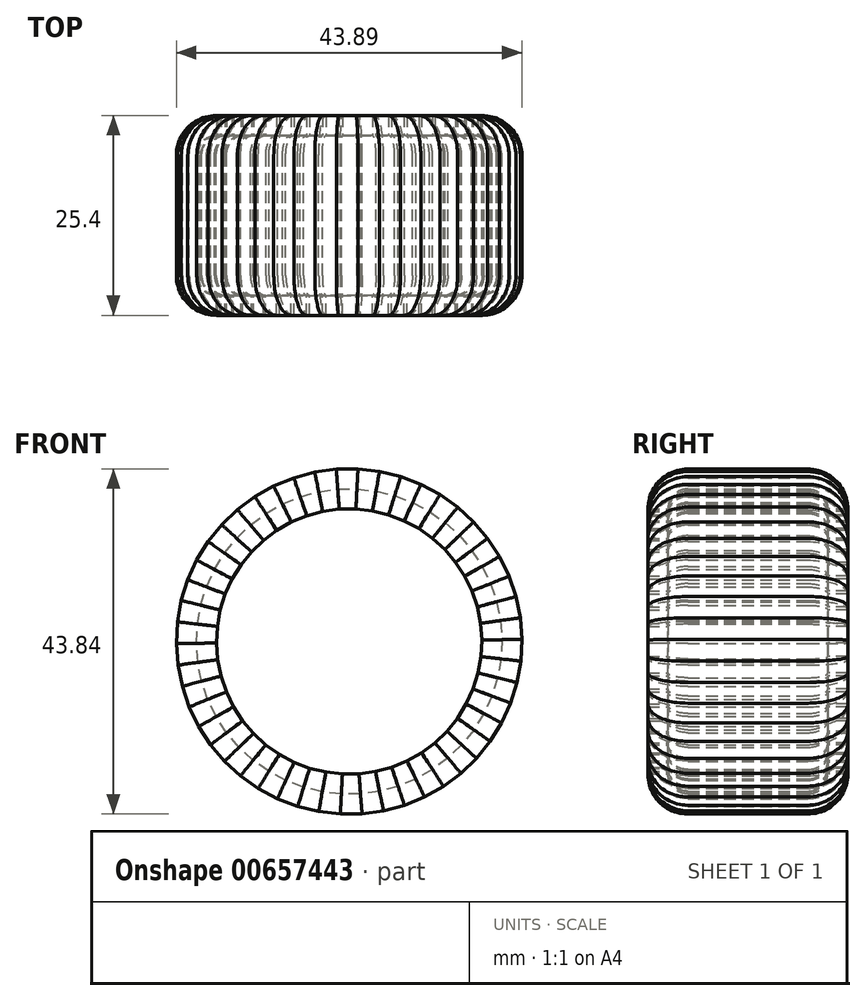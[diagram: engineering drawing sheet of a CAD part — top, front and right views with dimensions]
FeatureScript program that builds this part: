
annotation { "Feature Type Name" : "Feature", "Feature Type Description" : "" }
export const myFeature = defineFeature(function(context is Context, id is Id, definition is map)
    precondition{}
    {
        {
            var Q0;
            Q0=qCreatedBy(makeId("Front.planeOp"),FACE);
            var sketch = newSketch(context, id + "F0", { "sketchPlane" : qUnion([Q0])});
            skCircle(sketch, "E0.cCircle", {"center": v(-63.85, 53.38) * mm, "radius": 21.95 * mm, "construction": true});
            skLineSegment(sketch, "E0.0", {"start": v(-49.66, 36.63) * mm, "end": v(-51.87, 34.99) * mm});
            skLineSegment(sketch, "E0.1", {"start": v(-51.87, 34.99) * mm, "end": v(-54.27, 33.63) * mm});
            skLineSegment(sketch, "E0.2", {"start": v(-54.27, 33.63) * mm, "end": v(-56.82, 32.59) * mm});
            skLineSegment(sketch, "E0.3", {"start": v(-56.82, 32.59) * mm, "end": v(-59.48, 31.87) * mm});
            skLineSegment(sketch, "E0.4", {"start": v(-59.48, 31.87) * mm, "end": v(-62.21, 31.5) * mm});
            skLineSegment(sketch, "E0.5", {"start": v(-62.21, 31.5) * mm, "end": v(-64.97, 31.46) * mm});
            skLineSegment(sketch, "E0.6", {"start": v(-64.97, 31.46) * mm, "end": v(-67.7, 31.77) * mm});
            skLineSegment(sketch, "E0.7", {"start": v(-67.7, 31.77) * mm, "end": v(-70.38, 32.43) * mm});
            skLineSegment(sketch, "E0.8", {"start": v(-70.38, 32.43) * mm, "end": v(-72.96, 33.41) * mm});
            skLineSegment(sketch, "E0.9", {"start": v(-72.96, 33.41) * mm, "end": v(-75.39, 34.71) * mm});
            skLineSegment(sketch, "E0.10", {"start": v(-75.39, 34.71) * mm, "end": v(-77.64, 36.3) * mm});
            skLineSegment(sketch, "E0.11", {"start": v(-77.64, 36.3) * mm, "end": v(-79.67, 38.17) * mm});
            skLineSegment(sketch, "E0.12", {"start": v(-79.67, 38.17) * mm, "end": v(-81.45, 40.27) * mm});
            skLineSegment(sketch, "E0.13", {"start": v(-81.45, 40.27) * mm, "end": v(-82.95, 42.58) * mm});
            skLineSegment(sketch, "E0.14", {"start": v(-82.95, 42.58) * mm, "end": v(-84.16, 45.06) * mm});
            skLineSegment(sketch, "E0.15", {"start": v(-84.16, 45.06) * mm, "end": v(-85.04, 47.67) * mm});
            skLineSegment(sketch, "E0.16", {"start": v(-85.04, 47.67) * mm, "end": v(-85.59, 50.37) * mm});
            skLineSegment(sketch, "E0.17", {"start": v(-85.59, 50.37) * mm, "end": v(-85.8, 53.12) * mm});
            skLineSegment(sketch, "E0.18", {"start": v(-85.8, 53.12) * mm, "end": v(-85.65, 55.87) * mm});
            skLineSegment(sketch, "E0.19", {"start": v(-85.65, 55.87) * mm, "end": v(-85.17, 58.59) * mm});
            skLineSegment(sketch, "E0.20", {"start": v(-85.17, 58.59) * mm, "end": v(-84.35, 61.22) * mm});
            skLineSegment(sketch, "E0.21", {"start": v(-84.35, 61.22) * mm, "end": v(-83.2, 63.73) * mm});
            skLineSegment(sketch, "E0.22", {"start": v(-83.2, 63.73) * mm, "end": v(-81.75, 66.07) * mm});
            skLineSegment(sketch, "E0.23", {"start": v(-81.75, 66.07) * mm, "end": v(-80.02, 68.21) * mm});
            skLineSegment(sketch, "E0.24", {"start": v(-80.02, 68.21) * mm, "end": v(-78.03, 70.13) * mm});
            skLineSegment(sketch, "E0.25", {"start": v(-78.03, 70.13) * mm, "end": v(-75.82, 71.77) * mm});
            skLineSegment(sketch, "E0.26", {"start": v(-75.82, 71.77) * mm, "end": v(-73.42, 73.13) * mm});
            skLineSegment(sketch, "E0.27", {"start": v(-73.42, 73.13) * mm, "end": v(-70.87, 74.17) * mm});
            skLineSegment(sketch, "E0.28", {"start": v(-70.87, 74.17) * mm, "end": v(-68.21, 74.89) * mm});
            skLineSegment(sketch, "E0.29", {"start": v(-68.21, 74.89) * mm, "end": v(-65.48, 75.27) * mm});
            skLineSegment(sketch, "E0.30", {"start": v(-65.48, 75.27) * mm, "end": v(-62.72, 75.3) * mm});
            skLineSegment(sketch, "E0.31", {"start": v(-62.72, 75.3) * mm, "end": v(-59.99, 74.99) * mm});
            skLineSegment(sketch, "E0.32", {"start": v(-59.99, 74.99) * mm, "end": v(-57.3, 74.33) * mm});
            skLineSegment(sketch, "E0.33", {"start": v(-57.3, 74.33) * mm, "end": v(-54.73, 73.35) * mm});
            skLineSegment(sketch, "E0.34", {"start": v(-54.73, 73.35) * mm, "end": v(-52.3, 72.05) * mm});
            skLineSegment(sketch, "E0.35", {"start": v(-52.3, 72.05) * mm, "end": v(-50.05, 70.45) * mm});
            skLineSegment(sketch, "E0.36", {"start": v(-50.05, 70.45) * mm, "end": v(-48.02, 68.6) * mm});
            skLineSegment(sketch, "E0.37", {"start": v(-48.02, 68.6) * mm, "end": v(-46.24, 66.49) * mm});
            skLineSegment(sketch, "E0.38", {"start": v(-46.24, 66.49) * mm, "end": v(-44.74, 64.18) * mm});
            skLineSegment(sketch, "E0.39", {"start": v(-44.74, 64.18) * mm, "end": v(-43.53, 61.7) * mm});
            skLineSegment(sketch, "E0.40", {"start": v(-43.53, 61.7) * mm, "end": v(-42.65, 59.09) * mm});
            skLineSegment(sketch, "E0.41", {"start": v(-42.65, 59.09) * mm, "end": v(-42.1, 56.38) * mm});
            skLineSegment(sketch, "E0.42", {"start": v(-42.1, 56.38) * mm, "end": v(-41.9, 53.64) * mm});
            skLineSegment(sketch, "E0.43", {"start": v(-41.9, 53.64) * mm, "end": v(-42.04, 50.88) * mm});
            skLineSegment(sketch, "E0.44", {"start": v(-42.04, 50.88) * mm, "end": v(-42.52, 48.17) * mm});
            skLineSegment(sketch, "E0.45", {"start": v(-42.52, 48.17) * mm, "end": v(-43.34, 45.54) * mm});
            skLineSegment(sketch, "E0.46", {"start": v(-43.34, 45.54) * mm, "end": v(-44.49, 43.03) * mm});
            skLineSegment(sketch, "E0.47", {"start": v(-44.49, 43.03) * mm, "end": v(-45.94, 40.69) * mm});
            skLineSegment(sketch, "E0.48", {"start": v(-45.94, 40.69) * mm, "end": v(-47.67, 38.54) * mm});
            skLineSegment(sketch, "E0.49", {"start": v(-47.67, 38.54) * mm, "end": v(-49.66, 36.63) * mm});
            skSolve(sketch);
        }
        {
            var Q0;
            Q0 = qSketchRegion(id + "F0", true);
            extrude(context, id + "F1", {"entities" : qUnion([Q0]), "depth" : 25.4 * mm, "offsetDistance" : 25.4 * mm});
        }
        {
            var Q0;
            Q0=makeQuery(id+"F1.opExtrude","CAP_FACE",FACE,{"disambiguationData":[OSD([sQuery(id+"F0.wireOp",EDGE,"E0.0"),sQuery(id+"F0.wireOp",EDGE,"E0.1"),sQuery(id+"F0.wireOp",EDGE,"E0.2"),sQuery(id+"F0.wireOp",EDGE,"E0.3"),sQuery(id+"F0.wireOp",EDGE,"E0.4"),sQuery(id+"F0.wireOp",EDGE,"E0.5"),sQuery(id+"F0.wireOp",EDGE,"E0.6"),sQuery(id+"F0.wireOp",EDGE,"E0.7"),sQuery(id+"F0.wireOp",EDGE,"E0.8"),sQuery(id+"F0.wireOp",EDGE,"E0.9"),sQuery(id+"F0.wireOp",EDGE,"E0.10"),sQuery(id+"F0.wireOp",EDGE,"E0.11"),sQuery(id+"F0.wireOp",EDGE,"E0.12"),sQuery(id+"F0.wireOp",EDGE,"E0.13"),sQuery(id+"F0.wireOp",EDGE,"E0.14"),sQuery(id+"F0.wireOp",EDGE,"E0.15"),sQuery(id+"F0.wireOp",EDGE,"E0.16"),sQuery(id+"F0.wireOp",EDGE,"E0.17"),sQuery(id+"F0.wireOp",EDGE,"E0.18"),sQuery(id+"F0.wireOp",EDGE,"E0.19"),sQuery(id+"F0.wireOp",EDGE,"E0.20"),sQuery(id+"F0.wireOp",EDGE,"E0.21"),sQuery(id+"F0.wireOp",EDGE,"E0.22"),sQuery(id+"F0.wireOp",EDGE,"E0.23"),sQuery(id+"F0.wireOp",EDGE,"E0.24"),sQuery(id+"F0.wireOp",EDGE,"E0.25"),sQuery(id+"F0.wireOp",EDGE,"E0.26"),sQuery(id+"F0.wireOp",EDGE,"E0.27"),sQuery(id+"F0.wireOp",EDGE,"E0.28"),sQuery(id+"F0.wireOp",EDGE,"E0.29"),sQuery(id+"F0.wireOp",EDGE,"E0.30"),sQuery(id+"F0.wireOp",EDGE,"E0.31"),sQuery(id+"F0.wireOp",EDGE,"E0.32"),sQuery(id+"F0.wireOp",EDGE,"E0.33"),sQuery(id+"F0.wireOp",EDGE,"E0.34"),sQuery(id+"F0.wireOp",EDGE,"E0.35"),sQuery(id+"F0.wireOp",EDGE,"E0.36"),sQuery(id+"F0.wireOp",EDGE,"E0.37"),sQuery(id+"F0.wireOp",EDGE,"E0.38"),sQuery(id+"F0.wireOp",EDGE,"E0.39"),sQuery(id+"F0.wireOp",EDGE,"E0.40"),sQuery(id+"F0.wireOp",EDGE,"E0.41"),sQuery(id+"F0.wireOp",EDGE,"E0.42"),sQuery(id+"F0.wireOp",EDGE,"E0.43"),sQuery(id+"F0.wireOp",EDGE,"E0.44"),sQuery(id+"F0.wireOp",EDGE,"E0.45"),sQuery(id+"F0.wireOp",EDGE,"E0.46"),sQuery(id+"F0.wireOp",EDGE,"E0.47"),sQuery(id+"F0.wireOp",EDGE,"E0.48"),sQuery(id+"F0.wireOp",EDGE,"E0.49")])],"isStart":false});
            var Q1;
            Q1=makeQuery(id+"F1.opExtrude","CAP_FACE",FACE,{"disambiguationData":[OSD([sQuery(id+"F0.wireOp",EDGE,"E0.0"),sQuery(id+"F0.wireOp",EDGE,"E0.1"),sQuery(id+"F0.wireOp",EDGE,"E0.2"),sQuery(id+"F0.wireOp",EDGE,"E0.3"),sQuery(id+"F0.wireOp",EDGE,"E0.4"),sQuery(id+"F0.wireOp",EDGE,"E0.5"),sQuery(id+"F0.wireOp",EDGE,"E0.6"),sQuery(id+"F0.wireOp",EDGE,"E0.7"),sQuery(id+"F0.wireOp",EDGE,"E0.8"),sQuery(id+"F0.wireOp",EDGE,"E0.9"),sQuery(id+"F0.wireOp",EDGE,"E0.10"),sQuery(id+"F0.wireOp",EDGE,"E0.11"),sQuery(id+"F0.wireOp",EDGE,"E0.12"),sQuery(id+"F0.wireOp",EDGE,"E0.13"),sQuery(id+"F0.wireOp",EDGE,"E0.14"),sQuery(id+"F0.wireOp",EDGE,"E0.15"),sQuery(id+"F0.wireOp",EDGE,"E0.16"),sQuery(id+"F0.wireOp",EDGE,"E0.17"),sQuery(id+"F0.wireOp",EDGE,"E0.18"),sQuery(id+"F0.wireOp",EDGE,"E0.19"),sQuery(id+"F0.wireOp",EDGE,"E0.20"),sQuery(id+"F0.wireOp",EDGE,"E0.21"),sQuery(id+"F0.wireOp",EDGE,"E0.22"),sQuery(id+"F0.wireOp",EDGE,"E0.23"),sQuery(id+"F0.wireOp",EDGE,"E0.24"),sQuery(id+"F0.wireOp",EDGE,"E0.25"),sQuery(id+"F0.wireOp",EDGE,"E0.26"),sQuery(id+"F0.wireOp",EDGE,"E0.27"),sQuery(id+"F0.wireOp",EDGE,"E0.28"),sQuery(id+"F0.wireOp",EDGE,"E0.29"),sQuery(id+"F0.wireOp",EDGE,"E0.30"),sQuery(id+"F0.wireOp",EDGE,"E0.31"),sQuery(id+"F0.wireOp",EDGE,"E0.32"),sQuery(id+"F0.wireOp",EDGE,"E0.33"),sQuery(id+"F0.wireOp",EDGE,"E0.34"),sQuery(id+"F0.wireOp",EDGE,"E0.35"),sQuery(id+"F0.wireOp",EDGE,"E0.36"),sQuery(id+"F0.wireOp",EDGE,"E0.37"),sQuery(id+"F0.wireOp",EDGE,"E0.38"),sQuery(id+"F0.wireOp",EDGE,"E0.39"),sQuery(id+"F0.wireOp",EDGE,"E0.40"),sQuery(id+"F0.wireOp",EDGE,"E0.41"),sQuery(id+"F0.wireOp",EDGE,"E0.42"),sQuery(id+"F0.wireOp",EDGE,"E0.43"),sQuery(id+"F0.wireOp",EDGE,"E0.44"),sQuery(id+"F0.wireOp",EDGE,"E0.45"),sQuery(id+"F0.wireOp",EDGE,"E0.46"),sQuery(id+"F0.wireOp",EDGE,"E0.47"),sQuery(id+"F0.wireOp",EDGE,"E0.48"),sQuery(id+"F0.wireOp",EDGE,"E0.49")])],"isStart":true});
            fillet(context, id + "F2", {"entities" : qUnion([Q0, Q1]), "radius" : 5.08 * mm, "tangentPropagation" : true, "allowEdgeOverflow" : false});
        }
        {
            var Q0;
            Q0=makeQuery(id+"F1.opExtrude","CAP_FACE",FACE,{"disambiguationData":[OSD([sQuery(id+"F0.wireOp",EDGE,"E0.0"),sQuery(id+"F0.wireOp",EDGE,"E0.1"),sQuery(id+"F0.wireOp",EDGE,"E0.2"),sQuery(id+"F0.wireOp",EDGE,"E0.3"),sQuery(id+"F0.wireOp",EDGE,"E0.4"),sQuery(id+"F0.wireOp",EDGE,"E0.5"),sQuery(id+"F0.wireOp",EDGE,"E0.6"),sQuery(id+"F0.wireOp",EDGE,"E0.7"),sQuery(id+"F0.wireOp",EDGE,"E0.8"),sQuery(id+"F0.wireOp",EDGE,"E0.9"),sQuery(id+"F0.wireOp",EDGE,"E0.10"),sQuery(id+"F0.wireOp",EDGE,"E0.11"),sQuery(id+"F0.wireOp",EDGE,"E0.12"),sQuery(id+"F0.wireOp",EDGE,"E0.13"),sQuery(id+"F0.wireOp",EDGE,"E0.14"),sQuery(id+"F0.wireOp",EDGE,"E0.15"),sQuery(id+"F0.wireOp",EDGE,"E0.16"),sQuery(id+"F0.wireOp",EDGE,"E0.17"),sQuery(id+"F0.wireOp",EDGE,"E0.18"),sQuery(id+"F0.wireOp",EDGE,"E0.19"),sQuery(id+"F0.wireOp",EDGE,"E0.20"),sQuery(id+"F0.wireOp",EDGE,"E0.21"),sQuery(id+"F0.wireOp",EDGE,"E0.22"),sQuery(id+"F0.wireOp",EDGE,"E0.23"),sQuery(id+"F0.wireOp",EDGE,"E0.24"),sQuery(id+"F0.wireOp",EDGE,"E0.25"),sQuery(id+"F0.wireOp",EDGE,"E0.26"),sQuery(id+"F0.wireOp",EDGE,"E0.27"),sQuery(id+"F0.wireOp",EDGE,"E0.28"),sQuery(id+"F0.wireOp",EDGE,"E0.29"),sQuery(id+"F0.wireOp",EDGE,"E0.30"),sQuery(id+"F0.wireOp",EDGE,"E0.31"),sQuery(id+"F0.wireOp",EDGE,"E0.32"),sQuery(id+"F0.wireOp",EDGE,"E0.33"),sQuery(id+"F0.wireOp",EDGE,"E0.34"),sQuery(id+"F0.wireOp",EDGE,"E0.35"),sQuery(id+"F0.wireOp",EDGE,"E0.36"),sQuery(id+"F0.wireOp",EDGE,"E0.37"),sQuery(id+"F0.wireOp",EDGE,"E0.38"),sQuery(id+"F0.wireOp",EDGE,"E0.39"),sQuery(id+"F0.wireOp",EDGE,"E0.40"),sQuery(id+"F0.wireOp",EDGE,"E0.41"),sQuery(id+"F0.wireOp",EDGE,"E0.42"),sQuery(id+"F0.wireOp",EDGE,"E0.43"),sQuery(id+"F0.wireOp",EDGE,"E0.44"),sQuery(id+"F0.wireOp",EDGE,"E0.45"),sQuery(id+"F0.wireOp",EDGE,"E0.46"),sQuery(id+"F0.wireOp",EDGE,"E0.47"),sQuery(id+"F0.wireOp",EDGE,"E0.48"),sQuery(id+"F0.wireOp",EDGE,"E0.49")])],"isStart":false});
            var Q1;
            Q1=makeQuery(id+"F1.opExtrude","CAP_FACE",FACE,{"disambiguationData":[OSD([sQuery(id+"F0.wireOp",EDGE,"E0.0"),sQuery(id+"F0.wireOp",EDGE,"E0.1"),sQuery(id+"F0.wireOp",EDGE,"E0.2"),sQuery(id+"F0.wireOp",EDGE,"E0.3"),sQuery(id+"F0.wireOp",EDGE,"E0.4"),sQuery(id+"F0.wireOp",EDGE,"E0.5"),sQuery(id+"F0.wireOp",EDGE,"E0.6"),sQuery(id+"F0.wireOp",EDGE,"E0.7"),sQuery(id+"F0.wireOp",EDGE,"E0.8"),sQuery(id+"F0.wireOp",EDGE,"E0.9"),sQuery(id+"F0.wireOp",EDGE,"E0.10"),sQuery(id+"F0.wireOp",EDGE,"E0.11"),sQuery(id+"F0.wireOp",EDGE,"E0.12"),sQuery(id+"F0.wireOp",EDGE,"E0.13"),sQuery(id+"F0.wireOp",EDGE,"E0.14"),sQuery(id+"F0.wireOp",EDGE,"E0.15"),sQuery(id+"F0.wireOp",EDGE,"E0.16"),sQuery(id+"F0.wireOp",EDGE,"E0.17"),sQuery(id+"F0.wireOp",EDGE,"E0.18"),sQuery(id+"F0.wireOp",EDGE,"E0.19"),sQuery(id+"F0.wireOp",EDGE,"E0.20"),sQuery(id+"F0.wireOp",EDGE,"E0.21"),sQuery(id+"F0.wireOp",EDGE,"E0.22"),sQuery(id+"F0.wireOp",EDGE,"E0.23"),sQuery(id+"F0.wireOp",EDGE,"E0.24"),sQuery(id+"F0.wireOp",EDGE,"E0.25"),sQuery(id+"F0.wireOp",EDGE,"E0.26"),sQuery(id+"F0.wireOp",EDGE,"E0.27"),sQuery(id+"F0.wireOp",EDGE,"E0.28"),sQuery(id+"F0.wireOp",EDGE,"E0.29"),sQuery(id+"F0.wireOp",EDGE,"E0.30"),sQuery(id+"F0.wireOp",EDGE,"E0.31"),sQuery(id+"F0.wireOp",EDGE,"E0.32"),sQuery(id+"F0.wireOp",EDGE,"E0.33"),sQuery(id+"F0.wireOp",EDGE,"E0.34"),sQuery(id+"F0.wireOp",EDGE,"E0.35"),sQuery(id+"F0.wireOp",EDGE,"E0.36"),sQuery(id+"F0.wireOp",EDGE,"E0.37"),sQuery(id+"F0.wireOp",EDGE,"E0.38"),sQuery(id+"F0.wireOp",EDGE,"E0.39"),sQuery(id+"F0.wireOp",EDGE,"E0.40"),sQuery(id+"F0.wireOp",EDGE,"E0.41"),sQuery(id+"F0.wireOp",EDGE,"E0.42"),sQuery(id+"F0.wireOp",EDGE,"E0.43"),sQuery(id+"F0.wireOp",EDGE,"E0.44"),sQuery(id+"F0.wireOp",EDGE,"E0.45"),sQuery(id+"F0.wireOp",EDGE,"E0.46"),sQuery(id+"F0.wireOp",EDGE,"E0.47"),sQuery(id+"F0.wireOp",EDGE,"E0.48"),sQuery(id+"F0.wireOp",EDGE,"E0.49")])],"isStart":true});
            shell(context, id + "F3", {"entities" : qUnion([Q0, Q1]), "thickness" : 2.54 * mm});
        }
    });
